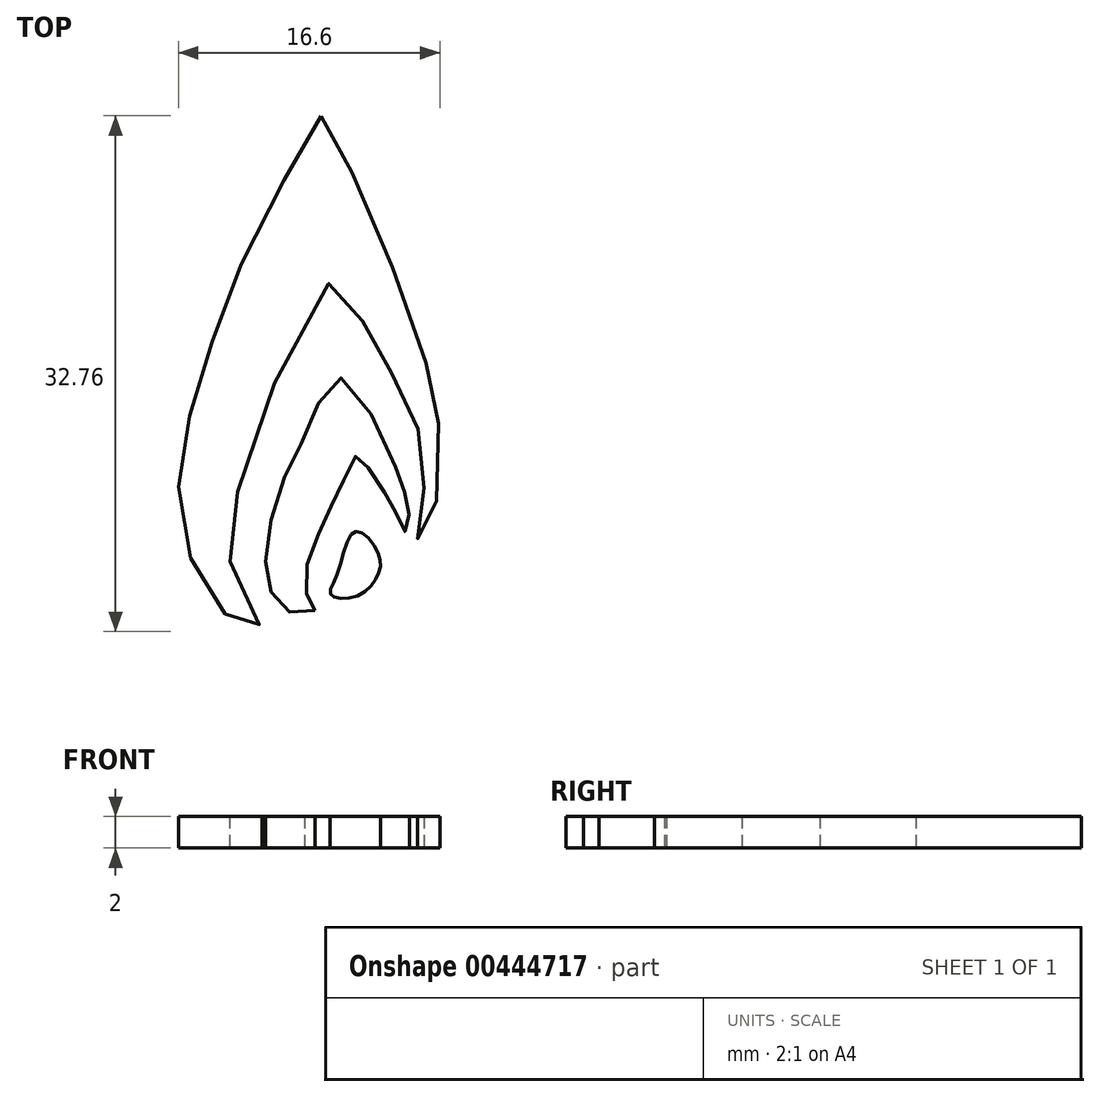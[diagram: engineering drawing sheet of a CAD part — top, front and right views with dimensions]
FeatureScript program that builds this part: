
annotation { "Feature Type Name" : "Feature", "Feature Type Description" : "" }
export const myFeature = defineFeature(function(context is Context, id is Id, definition is map)
    precondition{}
    {
        {
            var Q0;
            Q0=qCreatedBy(makeId("Top.planeOp"),FACE);
            var sketch = newSketch(context, id + "F0", { "sketchPlane" : qUnion([Q0])});
            skFitSpline(sketch, "E0", {"points": [v(-32.57, 3.12) * mm, v(-34.15, 3.02) * mm, v(-35.37, 4.38) * mm, v(-35.67, 6.94) * mm, v(-34.48, 11.6) * mm, v(-32.95, 14.8) * mm, v(-30.97, 17.9) * mm, v(-27.48, 12.3) * mm, v(-26.89, 10.64) * mm, v(-26.62, 9.55) * mm, v(-26.69, 8.07) * mm, v(-27.29, 8.84) * mm, v(-27.56, 9.71) * mm, v(-28.5, 11.07) * mm, v(-29.55, 12.7) * mm, v(-29.94, 12.95) * mm, v(-30.66, 11.6) * mm, v(-31.54, 9.72) * mm, v(-32.49, 7.66) * mm, v(-33.22, 5.2) * mm, v(-32.82, 3.56) * mm, v(-32.57, 3.12) * mm]});
            skFitSpline(sketch, "E1", {"points": [v(-31.17, 5.43) * mm, v(-30, 8.15) * mm, v(-28.61, 6.93) * mm, v(-28.54, 5.47) * mm, v(-29.88, 4.04) * mm, v(-31.54, 4.13) * mm, v(-31.17, 5.43) * mm]});
            skPoint(sketch, "E2.26.internal.orphan", {"position": v(-41.18, 11.6) * mm});
            skPoint(sketch, "E2.27.internal.orphan", {"position": v(-40.86, 8.84) * mm});
            skFitSpline(sketch, "E3", {"points": [v(-32.19, 34.54) * mm, v(-34.45, 30.64) * mm, v(-37.76, 24) * mm, v(-39.5, 18.86) * mm, v(-40.87, 14.11) * mm, v(-41.18, 9.92) * mm, v(-40.18, 5.7) * mm, v(-38.07, 2.76) * mm, v(-35.92, 1.82) * mm, v(-37.34, 3.98) * mm, v(-37.92, 8.2) * mm, v(-36.55, 13.66) * mm, v(-31.5, 24) * mm, v(-30.04, 22.44) * mm, v(-28.5, 19.67) * mm, v(-27.1, 17.04) * mm, v(-25.83, 13.98) * mm, v(-25.65, 11.02) * mm, v(-25.86, 8.84) * mm, v(-26.02, 7.42) * mm, v(-25, 9.46) * mm, v(-24.71, 14.75) * mm, v(-25.09, 17.25) * mm, v(-27.4, 24.26) * mm, v(-30.73, 32.2) * mm, v(-32.19, 34.54) * mm]});
            skSolve(sketch);
        }
        {
            var Q0;
            Q0 = qSketchRegion(id + "F0", true);
            extrude(context, id + "F1", {"entities" : qUnion([Q0]), "depth" : 2 * mm});
        }
        {
            var Q0;
            Q0 = qSketchRegion(id + "F0", true);
            extrude(context, id + "F2", {"entities" : qUnion([Q0]), "depth" : 2 * mm});
        }
        {
            var Q0;
            Q0 = qSketchRegion(id + "F0", true);
            extrude(context, id + "F3", {"entities" : qUnion([Q0]), "depth" : 2 * mm});
        }
        {
            var Q0;
            Q0 = qSketchRegion(id + "F0", true);
            extrude(context, id + "F4", {"entities" : qUnion([Q0]), "depth" : 2 * mm});
        }
    });
